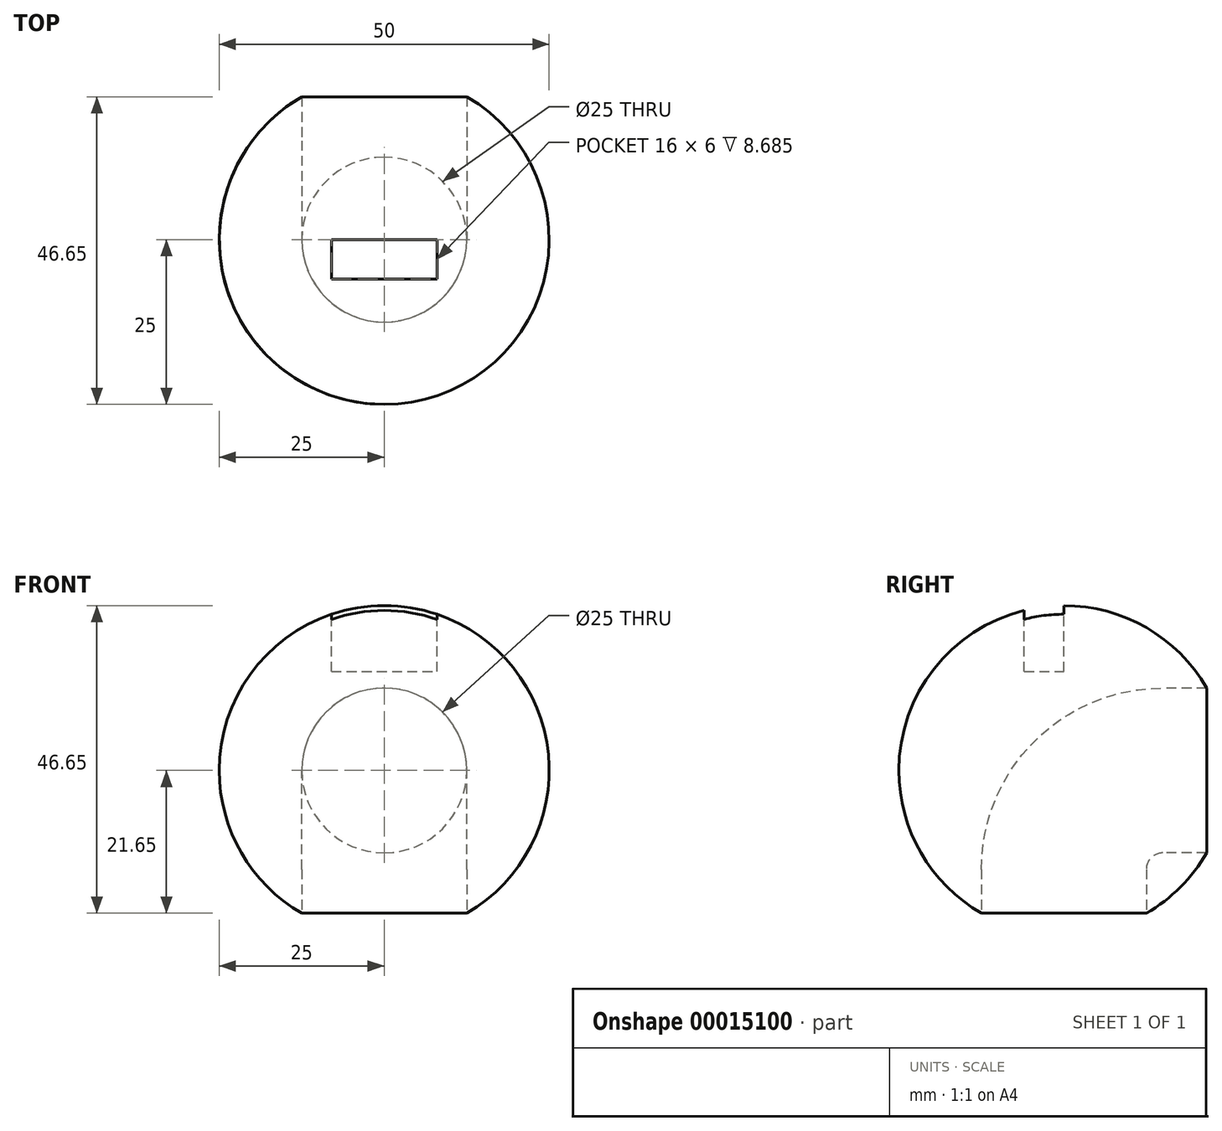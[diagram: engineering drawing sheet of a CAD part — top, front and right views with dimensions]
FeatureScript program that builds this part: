
annotation { "Feature Type Name" : "Feature", "Feature Type Description" : "" }
export const myFeature = defineFeature(function(context is Context, id is Id, definition is map)
    precondition{}
    {
        {
            var Q0;
            Q0=qCreatedBy(makeId("Top.planeOp"),FACE);
            var sketch = newSketch(context, id + "F0", { "sketchPlane" : qUnion([Q0])});
            skCircle(sketch, "E0", {"center": v(0, 0) * mm, "radius": 25 * mm});
            skLineSegment(sketch, "E1", {"start": v(0, 25) * mm, "end": v(0, -25) * mm});
            skSolve(sketch);
        }
        {
            var Q0;
            {var subQ0=sQuery(id+"F0.wireOp",EDGE,"E1");Q0=makeQuery(id+"F0.imprint","IMPRINT",FACE,{"disambiguationData":[TD([[makeQuery(id+"F0.imprint","IMPRINT",EDGE,{"derivedFrom":subQ0}),1.0]])]});}
            var Q1;
            Q1=sQuery(id+"F0.wireOp",EDGE,"E1");
            revolve(context, id + "F1", {"entities" : qUnion([Q0]), "axis" : qUnion([Q1]), "revolveType" : RevolveType.FULL});
        }
        {
            var Q0;
            Q0=qCreatedBy(makeId("Right.planeOp"),FACE);
            var sketch = newSketch(context, id + "F2", { "sketchPlane" : qUnion([Q0])});
            skLineSegment(sketch, "E2", {"start": v(0, 28.55) * mm, "end": v(0, -21.65) * mm, "construction": true});
            skLineSegment(sketch, "E3", {"start": v(21.65, 0) * mm, "end": v(-28.15, 0) * mm, "construction": true});
            skArc(sketch, "E4", {"start": v(12.5, -21.65) * mm, "mid": v(17.68, -17.68) * mm, "end": v(21.65, -12.5) * mm, "construction": true});
            skLineSegment(sketch, "E5", {"start": v(25, 0) * mm, "end": v(15, 0) * mm});
            skLineSegment(sketch, "E6", {"start": v(0, -15) * mm, "end": v(0, -25) * mm});
            skArc(sketch, "E7", {"start": v(15, 0) * mm, "mid": v(4.4, -4.4) * mm, "end": v(0, -15) * mm});
            skLineSegment(sketch, "E8", {"start": v(-12.5, -21.65) * mm, "end": v(12.5, -21.65) * mm});
            skLineSegment(sketch, "E9", {"start": v(21.65, 12.5) * mm, "end": v(21.65, -12.5) * mm});
            skArc(sketch, "E10.trimOffspring", {"start": v(21.65, 12.5) * mm, "mid": v(-17.68, 17.68) * mm, "end": v(-12.5, -21.65) * mm, "construction": true});
            skSolve(sketch);
        }
        {
            var Q0;
            Q0=sQuery(id+"F2.wireOp",VERTEX,"E5.start");
            var Q1;
            Q1=qCreatedBy(makeId("Front.planeOp"),FACE);
            cPlane(context, id + "F3", {"entities" : qUnion([Q0, Q1]), "cplaneType" : CPlaneType.PLANE_POINT, "offset" : 150 * mm, "width" : 150 * mm, "height" : 150 * mm});
        }
        {
            var Q0;
            Q0=qCreatedBy(id+"F3.planeOp",FACE);
            var sketch = newSketch(context, id + "F4", { "sketchPlane" : qUnion([Q0])});
            skCircle(sketch, "E11", {"center": v(0, 0) * mm, "radius": 12.5 * mm});
            skSolve(sketch);
        }
        {
            var Q0;
            Q0=makeQuery(id+"F4.imprint","IMPRINT",FACE,{"disambiguationData":[TD([[makeQuery(id+"F4.imprint","IMPRINT",EDGE,{"derivedFrom":sQuery(id+"F4.wireOp",EDGE,"E11")}),1.0]])]});
            var Q1;
            Q1=sQuery(id+"F2.wireOp",EDGE,"E7");
            var Q2;
            Q2=sQuery(id+"F2.wireOp",EDGE,"E5");
            var Q3;
            Q3=sQuery(id+"F2.wireOp",EDGE,"E6");
            sweep(context, id + "F5", {"operationType" : NewBodyOperationType.REMOVE, "profiles" : qUnion([Q0]), "path" : qUnion([Q1, Q2, Q3])});
        }
        {
            var Q0;
            Q0=qCreatedBy(makeId("Top.planeOp"),FACE);
            cPlane(context, id + "F6", {"entities" : qUnion([Q0]), "cplaneType" : CPlaneType.OFFSET, "offset" : 25 * mm, "width" : 150 * mm, "height" : 150 * mm});
        }
        {
            var Q0;
            Q0=qCreatedBy(id+"F6.planeOp",FACE);
            var sketch = newSketch(context, id + "F7", { "sketchPlane" : qUnion([Q0])});
            skLineSegment(sketch, "E12", {"start": v(-28.86, 0) * mm, "end": v(24.2, 0) * mm});
            skLineSegment(sketch, "E13.rect.bottom", {"start": v(8, -6) * mm, "end": v(-8, -6) * mm});
            skLineSegment(sketch, "E13.rect.top", {"start": v(8, 0) * mm, "end": v(-8, 0) * mm});
            skLineSegment(sketch, "E13.rect.left", {"start": v(8, -6) * mm, "end": v(8, 0) * mm});
            skLineSegment(sketch, "E13.rect.right", {"start": v(-8, -6) * mm, "end": v(-8, 0) * mm});
            skPoint(sketch, "E13.rect.middle", {"position": v(0, -3) * mm});
            skSolve(sketch);
        }
        {
            var Q0;
            Q0=makeQuery(id+"F7.imprint","IMPRINT",FACE,{"disambiguationData":[TD([[makeQuery(id+"F7.imprint","IMPRINT",EDGE,{"derivedFrom":sQuery(id+"F7.wireOp",EDGE,"E13.rect.bottom")}),-1.0]])]});
            extrude(context, id + "F8", {"entities" : qUnion([Q0]), "operationType" : NewBodyOperationType.REMOVE, "oppositeDirection" : true, "depth" : (25 - 15) * mm});
        }
    });
